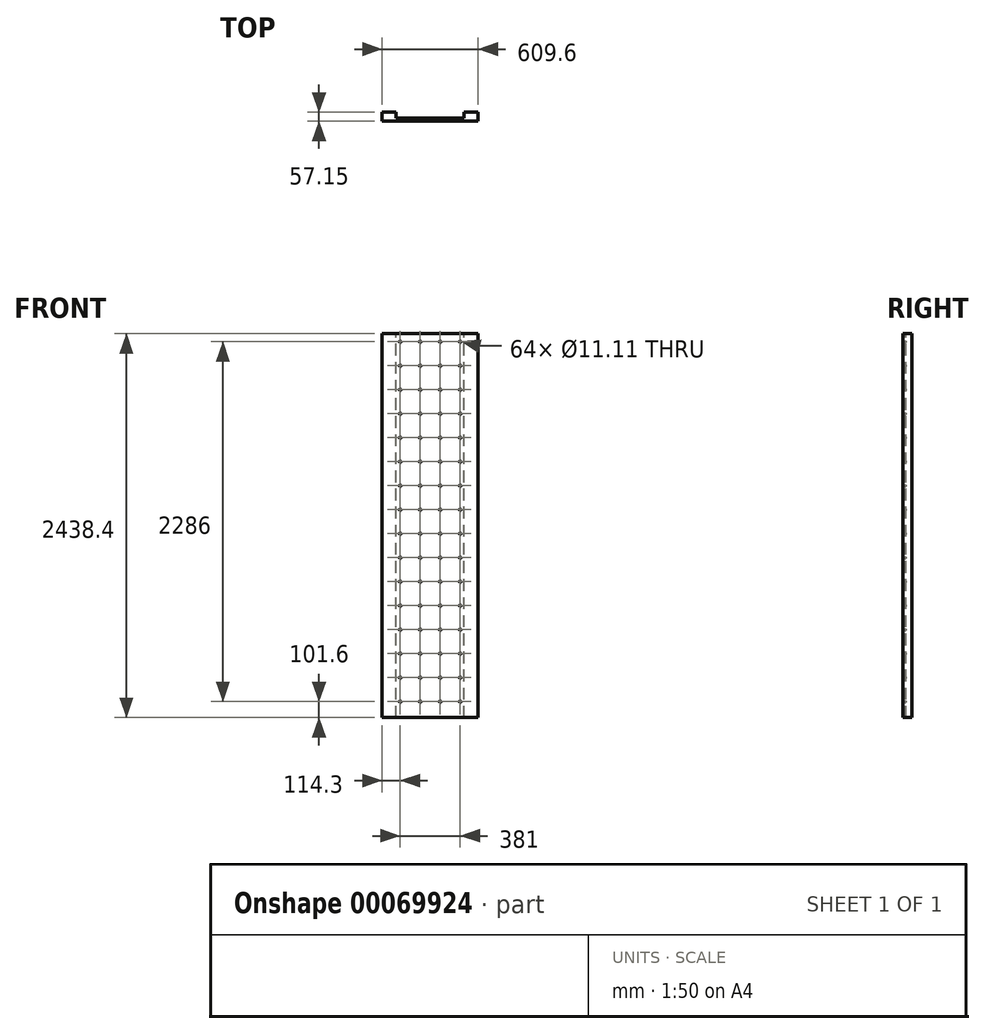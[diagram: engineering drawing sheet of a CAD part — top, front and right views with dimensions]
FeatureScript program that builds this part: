
annotation { "Feature Type Name" : "Feature", "Feature Type Description" : "" }
export const myFeature = defineFeature(function(context is Context, id is Id, definition is map)
    precondition{}
    {
        {
            var Q0;
            Q0=qCreatedBy(makeId("Front.planeOp"),FACE);
            var sketch = newSketch(context, id + "F0", { "sketchPlane" : qUnion([Q0])});
            skLineSegment(sketch, "E0.bottom", {"start": v(304.8, 609.6) * mm, "end": v(-304.8, 609.6) * mm});
            skLineSegment(sketch, "E0.top", {"start": v(304.8, -609.6) * mm, "end": v(-304.8, -609.6) * mm});
            skLineSegment(sketch, "E0.left", {"start": v(304.8, 609.6) * mm, "end": v(304.8, -609.6) * mm});
            skLineSegment(sketch, "E0.right", {"start": v(-304.8, 609.6) * mm, "end": v(-304.8, -609.6) * mm});
            skPoint(sketch, "E0.middle", {"position": v(0, 0) * mm});
            skLineSegment(sketch, "E1.top", {"start": v(304.8, 1828.8) * mm, "end": v(-304.8, 1828.8) * mm});
            skLineSegment(sketch, "E1.left", {"start": v(304.8, 609.6) * mm, "end": v(304.8, 1828.8) * mm});
            skLineSegment(sketch, "E1.right", {"start": v(-304.8, 609.6) * mm, "end": v(-304.8, 1828.8) * mm});
            skPoint(sketch, "E1.middle", {"position": v(0, 1219.2) * mm});
            skSolve(sketch);
        }
        {
            var Q0;
            Q0 = qSketchRegion(id + "F0", true);
            extrude(context, id + "F1", {"entities" : qUnion([Q0]), "depth" : 19.05 * mm, "offsetDistance" : 25.4 * mm});
        }
        {
            var Q0;
            Q0=makeQuery(id+"F1.opExtrude","SWEPT_FACE",FACE,{"disambiguationData":[OSD([sQuery(id+"F0.wireOp",EDGE,"E1.top")])]});
            var sketch = newSketch(context, id + "F2", { "sketchPlane" : qUnion([Q0])});
            skLineSegment(sketch, "E2.bottom", {"start": v(304.8, 0) * mm, "end": v(215.9, 0) * mm});
            skLineSegment(sketch, "E2.top", {"start": v(304.8, 38.1) * mm, "end": v(215.9, 38.1) * mm});
            skLineSegment(sketch, "E2.left", {"start": v(304.8, 0) * mm, "end": v(304.8, 38.1) * mm});
            skLineSegment(sketch, "E2.right", {"start": v(215.9, 0) * mm, "end": v(215.9, 38.1) * mm});
            skLineSegment(sketch, "E3.bottom", {"start": v(-304.8, 0) * mm, "end": v(-215.9, 0) * mm});
            skLineSegment(sketch, "E3.top", {"start": v(-304.8, 38.1) * mm, "end": v(-215.9, 38.1) * mm});
            skLineSegment(sketch, "E3.left", {"start": v(-304.8, 0) * mm, "end": v(-304.8, 38.1) * mm});
            skLineSegment(sketch, "E3.right", {"start": v(-215.9, 0) * mm, "end": v(-215.9, 38.1) * mm});
            skSolve(sketch);
        }
        {
            var Q0;
            Q0 = qSketchRegion(id + "F2", true);
            extrude(context, id + "F3", {"entities" : qUnion([Q0]), "oppositeDirection" : true, "depth" : 1219.2 * mm, "offsetDistance" : 25.4 * mm});
        }
        {
            var Q0;
            Q0 = qSketchRegion(id + "F2", true);
            extrude(context, id + "F4", {"entities" : qUnion([Q0]), "oppositeDirection" : true, "depth" : 2438.4 * mm, "offsetDistance" : 25.4 * mm, "hasSecondDirection" : true, "secondDirectionOppositeDirection" : true, "secondDirectionDepth" : 1219.2 * mm});
        }
        {
            var Q0;
            Q0=makeQuery(id+"F1.opExtrude","SWEPT_BODY",BODY,{"disambiguationData":[OSD([sQuery(id+"F0.wireOp",EDGE,"E0.top"),sQuery(id+"F0.wireOp",EDGE,"E0.left"),sQuery(id+"F0.wireOp",EDGE,"E0.right"),sQuery(id+"F0.wireOp",EDGE,"E1.top"),sQuery(id+"F0.wireOp",EDGE,"E1.left"),sQuery(id+"F0.wireOp",EDGE,"E1.right")])]});
            var Q1;
            Q1=makeQuery(id+"F3.opExtrude","SWEPT_BODY",BODY,{"disambiguationData":[OSD([sQuery(id+"F2.wireOp",EDGE,"E3.bottom"),sQuery(id+"F2.wireOp",EDGE,"E3.top"),sQuery(id+"F2.wireOp",EDGE,"E3.left"),sQuery(id+"F2.wireOp",EDGE,"E3.right")])]});
            var Q2;
            Q2=makeQuery(id+"F3.opExtrude","SWEPT_BODY",BODY,{"disambiguationData":[OSD([sQuery(id+"F2.wireOp",EDGE,"E2.bottom"),sQuery(id+"F2.wireOp",EDGE,"E2.top"),sQuery(id+"F2.wireOp",EDGE,"E2.left"),sQuery(id+"F2.wireOp",EDGE,"E2.right")])]});
            var Q3;
            Q3=makeQuery(id+"F4.opExtrude","SWEPT_BODY",BODY,{"disambiguationData":[OSD([sQuery(id+"F2.wireOp",EDGE,"E2.bottom"),sQuery(id+"F2.wireOp",EDGE,"E2.top"),sQuery(id+"F2.wireOp",EDGE,"E2.left"),sQuery(id+"F2.wireOp",EDGE,"E2.right")])]});
            var Q4;
            Q4=makeQuery(id+"F4.opExtrude","SWEPT_BODY",BODY,{"disambiguationData":[OSD([sQuery(id+"F2.wireOp",EDGE,"E3.bottom"),sQuery(id+"F2.wireOp",EDGE,"E3.top"),sQuery(id+"F2.wireOp",EDGE,"E3.left"),sQuery(id+"F2.wireOp",EDGE,"E3.right")])]});
            booleanBodies(context, id + "F5", {"operationType" : BooleanOperationType.UNION, "tools" : qUnion([Q0, Q1, Q2, Q3, Q4])});
        }
        {
            var Q0;
            Q0=makeQuery(id+"F1.opExtrude","CAP_FACE",FACE,{"disambiguationData":[OSD([sQuery(id+"F0.wireOp",EDGE,"E0.top"),sQuery(id+"F0.wireOp",EDGE,"E0.left"),sQuery(id+"F0.wireOp",EDGE,"E0.right"),sQuery(id+"F0.wireOp",EDGE,"E1.top"),sQuery(id+"F0.wireOp",EDGE,"E1.left"),sQuery(id+"F0.wireOp",EDGE,"E1.right")])],"isStart":true});
            var sketch = newSketch(context, id + "F6", { "sketchPlane" : qUnion([Q0])});
            skCircle(sketch, "E4", {"center": v(-190.5, 1778) * mm, "radius": 5.56 * mm});
            skCircle(sketch, "E5.0.1.0", {"center": v(-190.5, 1625.6) * mm, "radius": 5.56 * mm});
            skCircle(sketch, "E5.0.2.0", {"center": v(-190.5, 1473.2) * mm, "radius": 5.56 * mm});
            skCircle(sketch, "E5.0.3.0", {"center": v(-190.5, 1320.8) * mm, "radius": 5.56 * mm});
            skCircle(sketch, "E5.0.4.0", {"center": v(-190.5, 1168.4) * mm, "radius": 5.56 * mm});
            skCircle(sketch, "E5.1.0.0", {"center": v(-63.5, 1778) * mm, "radius": 5.56 * mm});
            skCircle(sketch, "E5.1.1.0", {"center": v(-63.5, 1625.6) * mm, "radius": 5.56 * mm});
            skCircle(sketch, "E5.1.2.0", {"center": v(-63.5, 1473.2) * mm, "radius": 5.56 * mm});
            skCircle(sketch, "E5.1.3.0", {"center": v(-63.5, 1320.8) * mm, "radius": 5.56 * mm});
            skCircle(sketch, "E5.1.4.0", {"center": v(-63.5, 1168.4) * mm, "radius": 5.56 * mm});
            skCircle(sketch, "E5.2.0.0", {"center": v(63.5, 1778) * mm, "radius": 5.56 * mm});
            skCircle(sketch, "E5.2.1.0", {"center": v(63.5, 1625.6) * mm, "radius": 5.56 * mm});
            skCircle(sketch, "E5.2.2.0", {"center": v(63.5, 1473.2) * mm, "radius": 5.56 * mm});
            skCircle(sketch, "E5.2.3.0", {"center": v(63.5, 1320.8) * mm, "radius": 5.56 * mm});
            skCircle(sketch, "E5.2.4.0", {"center": v(63.5, 1168.4) * mm, "radius": 5.56 * mm});
            skLineSegment(sketch, "E5.direction1", {"start": v(-190.5, 1778) * mm, "end": v(-63.5, 1778) * mm, "construction": true});
            skLineSegment(sketch, "E5.direction2", {"start": v(-190.5, 1778) * mm, "end": v(-190.5, 1625.6) * mm, "construction": true});
            skCircle(sketch, "E6.0.3.0", {"center": v(190.5, 1778) * mm, "radius": 5.56 * mm});
            skCircle(sketch, "E6.0.3.1", {"center": v(190.5, 1625.6) * mm, "radius": 5.56 * mm});
            skCircle(sketch, "E6.0.3.2", {"center": v(190.5, 1473.2) * mm, "radius": 5.56 * mm});
            skCircle(sketch, "E6.0.3.3", {"center": v(190.5, 1320.8) * mm, "radius": 5.56 * mm});
            skCircle(sketch, "E6.0.3.4", {"center": v(190.5, 1168.4) * mm, "radius": 5.56 * mm});
            skCircle(sketch, "E7.0.0.5", {"center": v(-190.5, 1016) * mm, "radius": 5.56 * mm});
            skCircle(sketch, "E7.0.0.6", {"center": v(-190.5, 863.6) * mm, "radius": 5.56 * mm});
            skCircle(sketch, "E7.0.0.7", {"center": v(-190.5, 711.2) * mm, "radius": 5.56 * mm});
            skCircle(sketch, "E7.0.0.8", {"center": v(-190.5, 558.8) * mm, "radius": 5.56 * mm});
            skCircle(sketch, "E7.0.0.9", {"center": v(-190.5, 406.4) * mm, "radius": 5.56 * mm});
            skCircle(sketch, "E7.0.0.10", {"center": v(-190.5, 254) * mm, "radius": 5.56 * mm});
            skCircle(sketch, "E7.0.0.11", {"center": v(-190.5, 101.6) * mm, "radius": 5.56 * mm});
            skCircle(sketch, "E7.0.0.12", {"center": v(-190.5, -50.8) * mm, "radius": 5.56 * mm});
            skCircle(sketch, "E7.0.0.13", {"center": v(-190.5, -203.2) * mm, "radius": 5.56 * mm});
            skCircle(sketch, "E7.0.0.14", {"center": v(-190.5, -355.6) * mm, "radius": 5.56 * mm});
            skCircle(sketch, "E7.0.1.5", {"center": v(-63.5, 1016) * mm, "radius": 5.56 * mm});
            skCircle(sketch, "E7.0.1.6", {"center": v(-63.5, 863.6) * mm, "radius": 5.56 * mm});
            skCircle(sketch, "E7.0.1.7", {"center": v(-63.5, 711.2) * mm, "radius": 5.56 * mm});
            skCircle(sketch, "E7.0.1.8", {"center": v(-63.5, 558.8) * mm, "radius": 5.56 * mm});
            skCircle(sketch, "E7.0.1.9", {"center": v(-63.5, 406.4) * mm, "radius": 5.56 * mm});
            skCircle(sketch, "E7.0.1.10", {"center": v(-63.5, 254) * mm, "radius": 5.56 * mm});
            skCircle(sketch, "E7.0.1.11", {"center": v(-63.5, 101.6) * mm, "radius": 5.56 * mm});
            skCircle(sketch, "E7.0.1.12", {"center": v(-63.5, -50.8) * mm, "radius": 5.56 * mm});
            skCircle(sketch, "E7.0.1.13", {"center": v(-63.5, -203.2) * mm, "radius": 5.56 * mm});
            skCircle(sketch, "E7.0.1.14", {"center": v(-63.5, -355.6) * mm, "radius": 5.56 * mm});
            skCircle(sketch, "E7.0.2.5", {"center": v(63.5, 1016) * mm, "radius": 5.56 * mm});
            skCircle(sketch, "E7.0.2.6", {"center": v(63.5, 863.6) * mm, "radius": 5.56 * mm});
            skCircle(sketch, "E7.0.2.7", {"center": v(63.5, 711.2) * mm, "radius": 5.56 * mm});
            skCircle(sketch, "E7.0.2.8", {"center": v(63.5, 558.8) * mm, "radius": 5.56 * mm});
            skCircle(sketch, "E7.0.2.9", {"center": v(63.5, 406.4) * mm, "radius": 5.56 * mm});
            skCircle(sketch, "E7.0.2.10", {"center": v(63.5, 254) * mm, "radius": 5.56 * mm});
            skCircle(sketch, "E7.0.2.11", {"center": v(63.5, 101.6) * mm, "radius": 5.56 * mm});
            skCircle(sketch, "E7.0.2.12", {"center": v(63.5, -50.8) * mm, "radius": 5.56 * mm});
            skCircle(sketch, "E7.0.2.13", {"center": v(63.5, -203.2) * mm, "radius": 5.56 * mm});
            skCircle(sketch, "E7.0.2.14", {"center": v(63.5, -355.6) * mm, "radius": 5.56 * mm});
            skCircle(sketch, "E7.0.3.5", {"center": v(190.5, 1016) * mm, "radius": 5.56 * mm});
            skCircle(sketch, "E7.0.3.6", {"center": v(190.5, 863.6) * mm, "radius": 5.56 * mm});
            skCircle(sketch, "E7.0.3.7", {"center": v(190.5, 711.2) * mm, "radius": 5.56 * mm});
            skCircle(sketch, "E7.0.3.8", {"center": v(190.5, 558.8) * mm, "radius": 5.56 * mm});
            skCircle(sketch, "E7.0.3.9", {"center": v(190.5, 406.4) * mm, "radius": 5.56 * mm});
            skCircle(sketch, "E7.0.3.10", {"center": v(190.5, 254) * mm, "radius": 5.56 * mm});
            skCircle(sketch, "E7.0.3.11", {"center": v(190.5, 101.6) * mm, "radius": 5.56 * mm});
            skCircle(sketch, "E7.0.3.12", {"center": v(190.5, -50.8) * mm, "radius": 5.56 * mm});
            skCircle(sketch, "E7.0.3.13", {"center": v(190.5, -203.2) * mm, "radius": 5.56 * mm});
            skCircle(sketch, "E7.0.3.14", {"center": v(190.5, -355.6) * mm, "radius": 5.56 * mm});
            skCircle(sketch, "E8.0.0.15", {"center": v(-190.5, -508) * mm, "radius": 5.56 * mm});
            skCircle(sketch, "E8.0.1.15", {"center": v(-63.5, -508) * mm, "radius": 5.56 * mm});
            skCircle(sketch, "E8.0.2.15", {"center": v(63.5, -508) * mm, "radius": 5.56 * mm});
            skCircle(sketch, "E8.0.3.15", {"center": v(190.5, -508) * mm, "radius": 5.56 * mm});
            skSolve(sketch);
        }
        {
            var Q0;
            Q0 = qSketchRegion(id + "F6", true);
            extrude(context, id + "F7", {"entities" : qUnion([Q0]), "operationType" : NewBodyOperationType.REMOVE, "endBound" : BoundingType.THROUGH_ALL, "oppositeDirection" : true, "depth" : 25.4 * mm, "offsetDistance" : 25.4 * mm});
        }
    });
